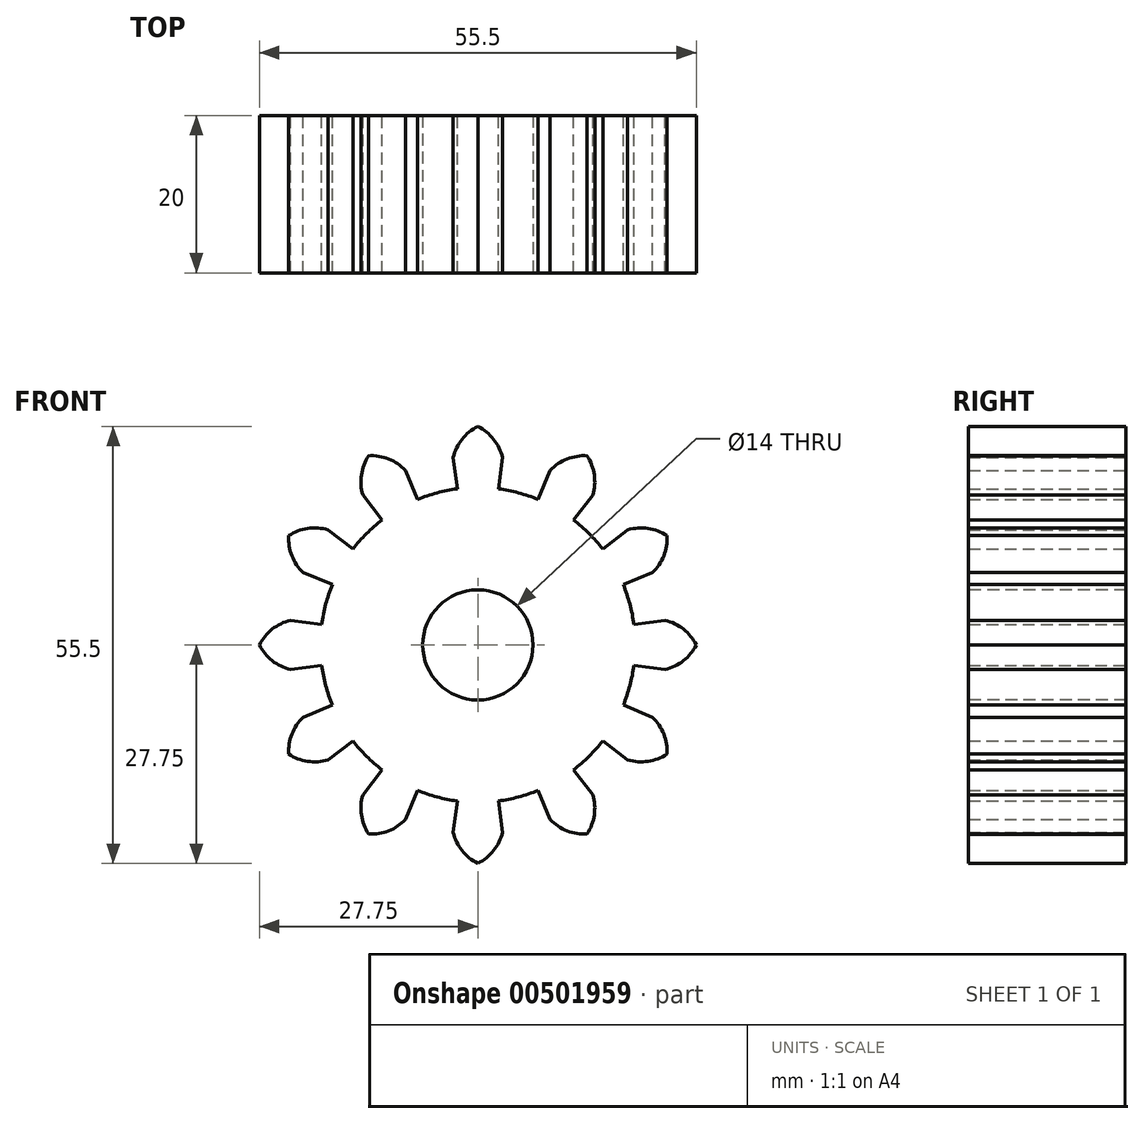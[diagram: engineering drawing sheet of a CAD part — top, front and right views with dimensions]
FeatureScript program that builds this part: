
annotation { "Feature Type Name" : "Feature", "Feature Type Description" : "" }
export const myFeature = defineFeature(function(context is Context, id is Id, definition is map)
    precondition{}
    {
        {
            assignVariable(context, id + "F0", {"name" : "N", "anyValue" : 12});
        }
        {
            var Q0;
            Q0=qCreatedBy(makeId("Front.planeOp"),FACE);
            var sketch = newSketch(context, id + "F1", { "sketchPlane" : qUnion([Q0])});
            skCircle(sketch, "E0", {"center": v(0, 0) * mm, "radius": 20 * mm});
            skCircle(sketch, "E1", {"center": v(0, 0) * mm, "radius": 24 * mm, "construction": true});
            skCircle(sketch, "E2", {"center": v(0, 0) * mm, "radius": 28 * mm, "construction": true});
            skLineSegment(sketch, "E3", {"start": v(3.13, 23.8) * mm, "end": v(-53.59, 31.26) * mm, "construction": true});
            skLineSegment(sketch, "E4", {"start": v(-55.6, 10.77) * mm, "end": v(3.13, 23.8) * mm, "construction": true});
            skCircle(sketch, "E5", {"center": v(0, 0) * mm, "radius": 22.55 * mm, "construction": true});
            skCircle(sketch, "E6", {"center": v(3.13, 23.8) * mm, "radius": 6 * mm, "construction": true});
            skCircle(sketch, "E7", {"center": v(-2.7, 22.4) * mm, "radius": 6 * mm, "construction": true});
            skLineSegment(sketch, "E8", {"start": v(0, 0) * mm, "end": v(-11.02, 83.68) * mm, "construction": true});
            skLineSegment(sketch, "E9", {"start": v(-11.02, 83.68) * mm, "end": v(11.02, 83.68) * mm, "construction": true});
            skLineSegment(sketch, "E10", {"start": v(11.02, 83.68) * mm, "end": v(0, 0) * mm, "construction": true});
            skLineSegment(sketch, "E11", {"start": v(0, 0) * mm, "end": v(0, 83.68) * mm, "construction": true});
            skLineSegment(sketch, "E12", {"start": v(2.61, 19.83) * mm, "end": v(3.13, 23.8) * mm});
            skArc(sketch, "E13", {"start": v(3.13, 23.8) * mm, "mid": v(1.8, 26.35) * mm, "end": v(-0.56, 28) * mm});
            skArc(sketch, "E14", {"start": v(-0.56, 28) * mm, "mid": v(0.28, -28) * mm, "end": v(0, 28) * mm});
            skLineSegment(sketch, "E15.MirrorCS", {"start": v(-2.61, 19.83) * mm, "end": v(-3.13, 23.8) * mm});
            skArc(sketch, "E16.MirrorCS", {"start": v(-3.13, 23.8) * mm, "mid": v(-1.8, 26.35) * mm, "end": v(0.56, 28) * mm});
            skArc(sketch, "E17.MirrorCS", {"start": v(0.56, 28) * mm, "mid": v(-0.28, -28) * mm, "end": v(0, 28) * mm});
            skSolve(sketch);
        }
        {
            var Q0;
            {var subQ0=sQuery(id+"F1.wireOp",EDGE,"E0");var subQ1=makeQuery(id+"F1.imprint","INTERSECT",VERTEX,{"derivedFrom":[subQ0,sQuery(id+"F1.wireOp",EDGE,"E12")]});Q0=makeQuery(id+"F1.imprint","IMPRINT",FACE,{"disambiguationData":[TD([[makeQuery(id+"F1.imprint","IMPRINT",EDGE,{"disambiguationData":[TD([[subQ1,-1.0]])],"derivedFrom":subQ0}),1.0]])]});}
            var Q1;
            {var subQ0=sQuery(id+"F1.wireOp",EDGE,"E12");Q1=makeQuery(id+"F1.imprint","IMPRINT",FACE,{"disambiguationData":[TD([[makeQuery(id+"F1.imprint","IMPRINT",EDGE,{"derivedFrom":subQ0}),1.0]])]});}
            extrude(context, id + "F2", {"entities" : qUnion([Q0, Q1]), "depth" : 20 * mm, "symmetric" : true});
        }
        {
            var Q0;
            Q0=makeQuery(id+"F2.opExtrude","SWEPT_FACE",FACE,{"disambiguationData":[OSD([sQuery(id+"F1.wireOp",EDGE,"E12")])]});
            var Q1;
            Q1=makeQuery(id+"F2.opExtrude","SWEPT_FACE",FACE,{"disambiguationData":[OSD([sQuery(id+"F1.wireOp",EDGE,"E13")])]});
            var Q2;
            Q2=makeQuery(id+"F2.opExtrude","SWEPT_FACE",FACE,{"disambiguationData":[OSD([sQuery(id+"F1.wireOp",EDGE,"E16.MirrorCS")])]});
            var Q3;
            Q3=makeQuery(id+"F2.opExtrude","SWEPT_FACE",FACE,{"disambiguationData":[OSD([sQuery(id+"F1.wireOp",EDGE,"E15.MirrorCS")])]});
            var Q4;
            Q4=makeQuery(id+"F2.opExtrude","SWEPT_FACE",FACE,{"disambiguationData":[OSD([sQuery(id+"F1.wireOp",EDGE,"E0")])]});
            circularPattern(context, id + "F3", {"patternType" : PatternType.FACE, "faces" : qUnion([Q0, Q1, Q2, Q3]), "axis" : qUnion([Q4]), "angle" : 360 * degree, "instanceCount" : getVariable(context, 'N'), "equalSpace" : true});
        }
        {
            var Q0;
            Q0=makeQuery(id+"F2.opExtrude","CAP_FACE",FACE,{"disambiguationData":[OSD([sQuery(id+"F1.wireOp",EDGE,"E0"),sQuery(id+"F1.wireOp",EDGE,"E12"),sQuery(id+"F1.wireOp",EDGE,"E13"),sQuery(id+"F1.wireOp",EDGE,"E15.MirrorCS"),sQuery(id+"F1.wireOp",EDGE,"E16.MirrorCS")])],"isStart":false});
            var sketch = newSketch(context, id + "F4", { "sketchPlane" : qUnion([Q0])});
            skCircle(sketch, "E18", {"center": v(0, 0) * mm, "radius": 7 * mm});
            skSolve(sketch);
        }
        {
            var Q0;
            Q0=makeQuery(id+"F4.imprint","IMPRINT",FACE,{"disambiguationData":[TD([[makeQuery(id+"F4.imprint","IMPRINT",EDGE,{"derivedFrom":sQuery(id+"F4.wireOp",EDGE,"E18")}),1.0]])]});
            extrude(context, id + "F5", {"entities" : qUnion([Q0]), "operationType" : NewBodyOperationType.REMOVE, "endBound" : BoundingType.THROUGH_ALL, "oppositeDirection" : true, "depth" : 25 * mm});
        }
    });
